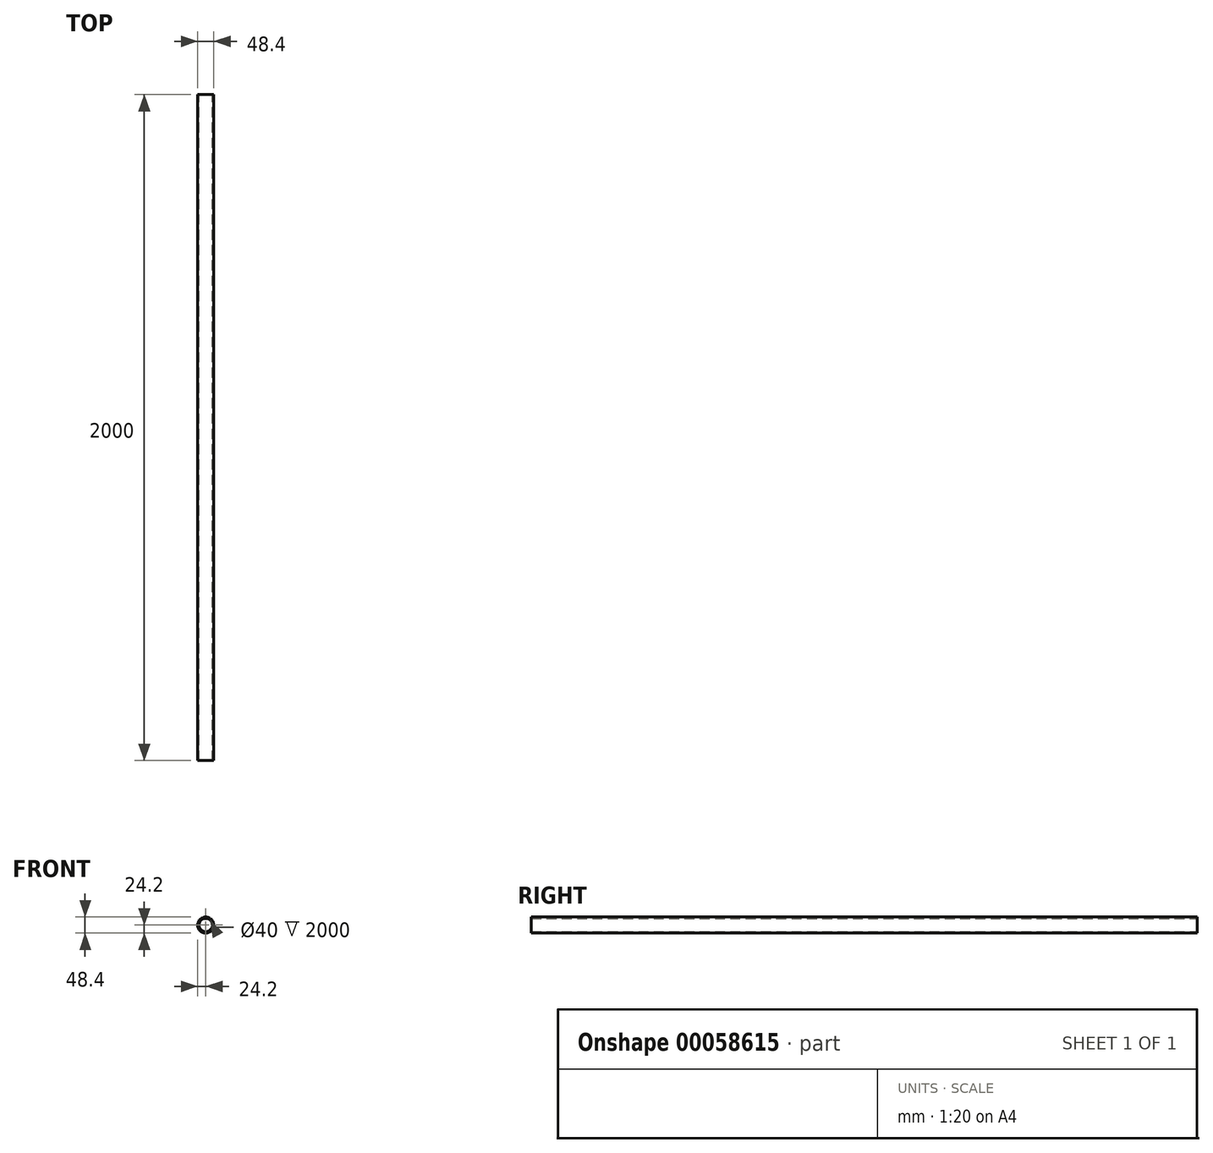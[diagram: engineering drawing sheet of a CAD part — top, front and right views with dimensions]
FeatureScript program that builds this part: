
annotation { "Feature Type Name" : "Feature", "Feature Type Description" : "" }
export const myFeature = defineFeature(function(context is Context, id is Id, definition is map)
    precondition{}
    {
        {
            var Q0;
            Q0=qCreatedBy(makeId("Front.planeOp"),FACE);
            var sketch = newSketch(context, id + "F0", { "sketchPlane" : qUnion([Q0])});
            skCircle(sketch, "E0", {"center": v(0, 0) * mm, "radius": 24.2 * mm});
            skCircle(sketch, "E1", {"center": v(0, 0) * mm, "radius": 20 * mm});
            skSolve(sketch);
        }
        {
            var Q0;
            Q0=makeQuery(id+"F0.imprint","IMPRINT",FACE,{"disambiguationData":[TD([[makeQuery(id+"F0.imprint","IMPRINT",EDGE,{"derivedFrom":sQuery(id+"F0.wireOp",EDGE,"E0")}),1.0]])]});
            extrude(context, id + "F1", {"entities" : qUnion([Q0]), "depth" : 2000 * mm});
        }
    });
